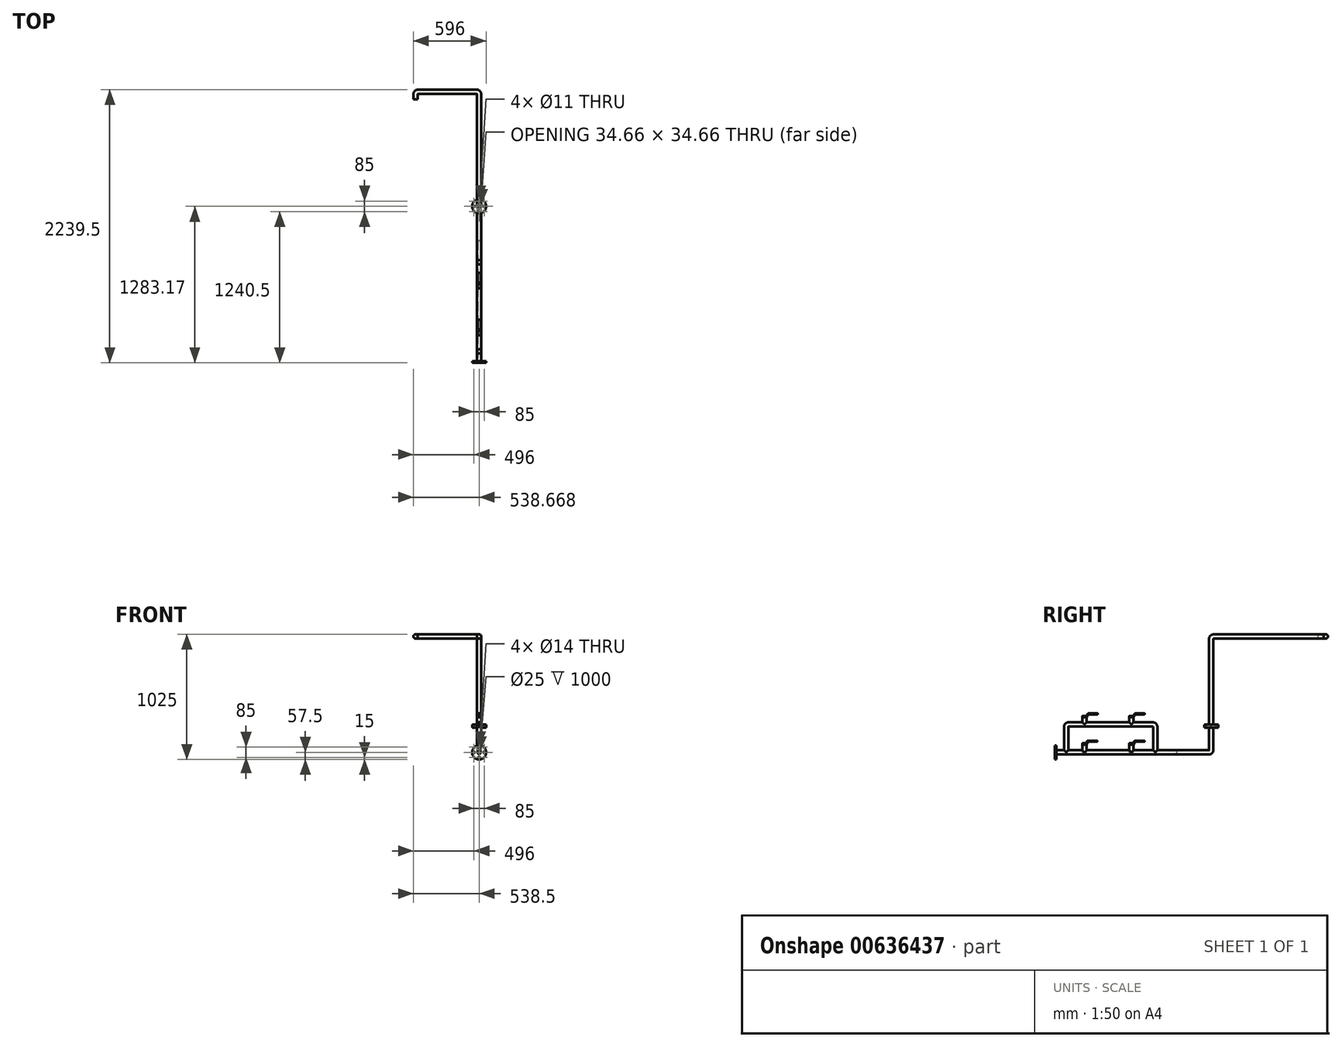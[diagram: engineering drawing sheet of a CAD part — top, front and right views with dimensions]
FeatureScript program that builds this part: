
annotation { "Feature Type Name" : "Feature", "Feature Type Description" : "" }
export const myFeature = defineFeature(function(context is Context, id is Id, definition is map)
    precondition{}
    {
        {
            var Q0;
            Q0=qCreatedBy(makeId("Front.planeOp"),FACE);
            var sketch = newSketch(context, id + "F0", { "sketchPlane" : qUnion([Q0])});
            skCircle(sketch, "E0", {"center": v(0, 0) * mm, "radius": 17.5 * mm});
            skSolve(sketch);
        }
        {
            var Q0;
            Q0=qCreatedBy(makeId("Top.planeOp"),FACE);
            var sketch = newSketch(context, id + "F1", { "sketchPlane" : qUnion([Q0])});
            skLineSegment(sketch, "E1", {"start": v(0, 0) * mm, "end": v(0, 43) * mm});
            skLineSegment(sketch, "E2", {"start": v(20, 63) * mm, "end": v(501, 63) * mm});
            skLineSegment(sketch, "E3", {"start": v(521, 43) * mm, "end": v(521, -876) * mm});
            skPoint(sketch, "E4.visualSharp", {"position": v(0, 63) * mm});
            skArc(sketch, "E4.filletArc", {"start": v(20, 63) * mm, "mid": v(5.86, 57.14) * mm, "end": v(0, 43) * mm});
            skPoint(sketch, "E5.visualSharp", {"position": v(521, 63) * mm});
            skArc(sketch, "E5.filletArc", {"start": v(521, 43) * mm, "mid": v(515.14, 57.14) * mm, "end": v(501, 63) * mm});
            skSolve(sketch);
        }
        {
            var Q0;
            Q0=qCreatedBy(makeId("Right.planeOp"),FACE);
            cPlane(context, id + "F2", {"entities" : qUnion([Q0]), "cplaneType" : CPlaneType.OFFSET, "offset" : 521 * mm, "width" : 150 * mm, "height" : 150 * mm});
        }
        {
            var Q0;
            Q0=qCreatedBy(id+"F2.planeOp",FACE);
            var sketch = newSketch(context, id + "F3", { "sketchPlane" : qUnion([Q0])});
            skLineSegment(sketch, "E6.0", {"start": v(43, 0) * mm, "end": v(-856, 0) * mm});
            skLineSegment(sketch, "E7", {"start": v(-876, -20) * mm, "end": v(-876, -930) * mm});
            skLineSegment(sketch, "E8", {"start": v(-896, -950) * mm, "end": v(-2159, -950) * mm});
            skLineSegment(sketch, "E9", {"start": v(-2065, -950) * mm, "end": v(-2065, -741) * mm});
            skLineSegment(sketch, "E10", {"start": v(-2045, -721) * mm, "end": v(-1355, -721) * mm});
            skLineSegment(sketch, "E11", {"start": v(-1335, -741) * mm, "end": v(-1335, -950) * mm});
            skPoint(sketch, "E12.visualSharp", {"position": v(-876, 0) * mm});
            skArc(sketch, "E12.filletArc", {"start": v(-856, 0) * mm, "mid": v(-870.14, -5.86) * mm, "end": v(-876, -20) * mm});
            skPoint(sketch, "E13.visualSharp", {"position": v(-876, -950) * mm});
            skArc(sketch, "E13.filletArc", {"start": v(-896, -950) * mm, "mid": v(-881.86, -944.14) * mm, "end": v(-876, -930) * mm});
            skPoint(sketch, "E14.visualSharp", {"position": v(-1335, -721) * mm});
            skArc(sketch, "E14.filletArc", {"start": v(-1335, -741) * mm, "mid": v(-1340.86, -726.86) * mm, "end": v(-1355, -721) * mm});
            skPoint(sketch, "E15.visualSharp", {"position": v(-2065, -721) * mm});
            skArc(sketch, "E15.filletArc", {"start": v(-2045, -721) * mm, "mid": v(-2059.14, -726.86) * mm, "end": v(-2065, -741) * mm});
            skSolve(sketch);
        }
        {
            var Q0;
            Q0=makeQuery(id+"F0.imprint","IMPRINT",FACE,{"disambiguationData":[TD([[makeQuery(id+"F0.imprint","IMPRINT",EDGE,{"derivedFrom":sQuery(id+"F0.wireOp",EDGE,"E0")}),1.0]])]});
            var Q1;
            Q1=sQuery(id+"F1.wireOp",EDGE,"E1");
            var Q2;
            Q2=sQuery(id+"F1.wireOp",EDGE,"E4.filletArc");
            var Q3;
            Q3=sQuery(id+"F1.wireOp",EDGE,"E2");
            var Q4;
            Q4=sQuery(id+"F1.wireOp",EDGE,"E5.filletArc");
            var Q5;
            Q5=sQuery(id+"F3.wireOp",EDGE,"E6.0");
            var Q6;
            Q6=sQuery(id+"F3.wireOp",EDGE,"E12.filletArc");
            var Q7;
            Q7=sQuery(id+"F3.wireOp",EDGE,"E7");
            var Q8;
            Q8=sQuery(id+"F3.wireOp",EDGE,"E13.filletArc");
            var Q9;
            Q9=sQuery(id+"F3.wireOp",EDGE,"E8");
            sweep(context, id + "F4", {"profiles" : qUnion([Q0]), "path" : qUnion([Q1, Q2, Q3, Q4, Q5, Q6, Q7, Q8, Q9])});
        }
        {
            var Q0;
            Q0=qCreatedBy(makeId("Top.planeOp"),FACE);
            cPlane(context, id + "F5", {"entities" : qUnion([Q0]), "cplaneType" : CPlaneType.OFFSET, "offset" : 886 * mm, "oppositeDirection" : true, "width" : 150 * mm, "height" : 150 * mm});
        }
        {
            var Q0;
            Q0=qCreatedBy(id+"F5.planeOp",FACE);
            var sketch = newSketch(context, id + "F6", { "sketchPlane" : qUnion([Q0])});
            skPoint(sketch, "E16.0", {"position": v(521, -2065) * mm});
            skPoint(sketch, "E17.0", {"position": v(521, -2059.14) * mm});
            skCircle(sketch, "E18", {"center": v(521, -2065) * mm, "radius": 17.5 * mm});
            skSolve(sketch);
        }
        {
            var Q0;
            Q0 = qSketchRegion(id + "F6", true);
            var Q1;
            Q1=sQuery(id+"F3.wireOp",EDGE,"E9");
            var Q2;
            Q2=sQuery(id+"F3.wireOp",EDGE,"E15.filletArc");
            var Q3;
            Q3=sQuery(id+"F3.wireOp",EDGE,"E10");
            var Q4;
            Q4=sQuery(id+"F3.wireOp",EDGE,"E14.filletArc");
            var Q5;
            Q5=sQuery(id+"F3.wireOp",EDGE,"E11");
            sweep(context, id + "F7", {"operationType" : NewBodyOperationType.ADD, "profiles" : qUnion([Q0]), "path" : qUnion([Q1, Q2, Q3, Q4, Q5])});
        }
        {
            var Q0;
            Q0=makeQuery(id+"F4.opSweep","CAP_FACE",FACE,{"disambiguationData":[OSD([sQuery(id+"F0.wireOp",EDGE,"E0"),sQuery(id+"F3.wireOp",VERTEX,"E8.end")])],"isStart":false});
            var sketch = newSketch(context, id + "F8", { "sketchPlane" : qUnion([Q0])});
            skCircle(sketch, "E19", {"center": v(521, -950) * mm, "radius": 57.5 * mm});
            skCircle(sketch, "E20", {"center": v(521, -907.5) * mm, "radius": 7 * mm});
            skCircle(sketch, "E21.1.0", {"center": v(478.5, -950) * mm, "radius": 7 * mm});
            skCircle(sketch, "E21.2.0", {"center": v(521, -992.5) * mm, "radius": 7 * mm});
            skCircle(sketch, "E21.3.0", {"center": v(563.5, -950) * mm, "radius": 7 * mm});
            skSolve(sketch);
        }
        {
            var Q0;
            Q0=makeQuery(id+"F8.imprint","IMPRINT",FACE,{"disambiguationData":[TD([[makeQuery(id+"F8.imprint","IMPRINT",EDGE,{"derivedFrom":sQuery(id+"F8.wireOp",EDGE,"E19")}),1.0]])]});
            extrude(context, id + "F9", {"entities" : qUnion([Q0]), "operationType" : NewBodyOperationType.ADD, "oppositeDirection" : true, "depth" : 15 * mm, "offsetDistance" : 25 * mm});
        }
        {
            var Q0;
            {var subQ0=sQuery(id+"F3.wireOp",VERTEX,"E8.end");var subQ1=sQuery(id+"F0.wireOp",EDGE,"E0");Q0=makeQuery(id+"F9.boolean.opBoolean","MERGE",FACE,{"derivedFrom":[makeQuery(id+"F4.opSweep","CAP_FACE",FACE,{"disambiguationData":[OSD([subQ1,subQ0])],"isStart":false}),makeQuery(id+"F9.opExtrude","CAP_FACE",FACE,{"disambiguationData":[OSD([subQ1,subQ0,sQuery(id+"F8.wireOp",EDGE,"E19"),sQuery(id+"F8.wireOp",EDGE,"E20"),sQuery(id+"F8.wireOp",EDGE,"E21.1.0"),sQuery(id+"F8.wireOp",EDGE,"E21.2.0"),sQuery(id+"F8.wireOp",EDGE,"E21.3.0")])],"isStart":true})]});}
            var sketch = newSketch(context, id + "F10", { "sketchPlane" : qUnion([Q0])});
            skCircle(sketch, "E22", {"center": v(521, -950) * mm, "radius": 12.5 * mm});
            skSolve(sketch);
        }
        {
            var Q0;
            Q0=makeQuery(id+"F10.imprint","IMPRINT",FACE,{"disambiguationData":[TD([[makeQuery(id+"F10.imprint","IMPRINT",EDGE,{"derivedFrom":sQuery(id+"F10.wireOp",EDGE,"E22")}),1.0]])]});
            extrude(context, id + "F11", {"entities" : qUnion([Q0]), "operationType" : NewBodyOperationType.REMOVE, "oppositeDirection" : true, "depth" : 1000 * mm, "offsetDistance" : 25 * mm});
        }
        {
            var Q0;
            Q0=qCreatedBy(id+"F5.planeOp",FACE);
            var sketch = newSketch(context, id + "F12", { "sketchPlane" : qUnion([Q0])});
            skCircle(sketch, "E23", {"center": v(521, -1915) * mm, "radius": 17.5 * mm});
            skCircle(sketch, "E24", {"center": v(521, -1530) * mm, "radius": 17.5 * mm});
            skSolve(sketch);
        }
        {
            var Q0;
            Q0 = qSketchRegion(id + "F12", true);
            extrude(context, id + "F13", {"entities" : qUnion([Q0]), "operationType" : NewBodyOperationType.ADD, "oppositeDirection" : true, "depth" : 64 * mm, "offsetDistance" : 25 * mm});
        }
        {
            var Q0;
            Q0=qCreatedBy(id+"F2.planeOp",FACE);
            var sketch = newSketch(context, id + "F14", { "sketchPlane" : qUnion([Q0])});
            skLineSegment(sketch, "E25.0.0", {"start": v(-2065, -950) * mm, "end": v(-1335, -950) * mm});
            skLineSegment(sketch, "E25.0.1", {"start": v(-1335, -950) * mm, "end": v(-1335, -741) * mm});
            skArc(sketch, "E25.0.2", {"start": v(-1335, -741) * mm, "mid": v(-1340.86, -726.86) * mm, "end": v(-1355, -721) * mm});
            skLineSegment(sketch, "E25.0.3", {"start": v(-1355, -721) * mm, "end": v(-2045, -721) * mm});
            skArc(sketch, "E25.0.4", {"start": v(-2045, -721) * mm, "mid": v(-2059.14, -726.86) * mm, "end": v(-2065, -741) * mm});
            skLineSegment(sketch, "E25.0.5", {"start": v(-2065, -741) * mm, "end": v(-2065, -950) * mm});
            skLineSegment(sketch, "E26.0", {"start": v(-1932.5, -886) * mm, "end": v(-1897.5, -886) * mm});
            skLineSegment(sketch, "E27", {"start": v(-1932.5, -886) * mm, "end": v(-1932.5, -876) * mm});
            skLineSegment(sketch, "E28", {"start": v(-1932.5, -876) * mm, "end": v(-1899.5, -876) * mm});
            skLineSegment(sketch, "E29", {"start": v(-1899.5, -876) * mm, "end": v(-1888.61, -853.8) * mm});
            skLineSegment(sketch, "E30", {"start": v(-1888.61, -853.8) * mm, "end": v(-1808.61, -853.8) * mm});
            skLineSegment(sketch, "E31", {"start": v(-1808.61, -853.8) * mm, "end": v(-1808.61, -861.8) * mm});
            skLineSegment(sketch, "E32", {"start": v(-1808.61, -861.8) * mm, "end": v(-1885.61, -861.8) * mm});
            skLineSegment(sketch, "E33", {"start": v(-1885.61, -861.8) * mm, "end": v(-1897.5, -886) * mm});
            skLineSegment(sketch, "E34.0", {"start": v(-1547.5, -886) * mm, "end": v(-1512.5, -886) * mm});
            skLineSegment(sketch, "E35", {"start": v(-1547.5, -886) * mm, "end": v(-1547.5, -876) * mm});
            skLineSegment(sketch, "E36", {"start": v(-1547.5, -876) * mm, "end": v(-1513.5, -876) * mm});
            skLineSegment(sketch, "E37", {"start": v(-1513.5, -876) * mm, "end": v(-1501.7, -855.1) * mm});
            skLineSegment(sketch, "E38", {"start": v(-1501.7, -855.1) * mm, "end": v(-1421.7, -855.1) * mm});
            skLineSegment(sketch, "E39", {"start": v(-1421.7, -855.1) * mm, "end": v(-1421.7, -863.1) * mm});
            skLineSegment(sketch, "E40", {"start": v(-1421.7, -863.1) * mm, "end": v(-1499.7, -863.1) * mm});
            skLineSegment(sketch, "E41", {"start": v(-1499.7, -863.1) * mm, "end": v(-1512.5, -886) * mm});
            skSolve(sketch);
        }
        {
            var Q0;
            Q0=makeQuery(id+"F14.imprint","IMPRINT",FACE,{"disambiguationData":[TD([[makeQuery(id+"F14.imprint","IMPRINT",EDGE,{"derivedFrom":sQuery(id+"F14.wireOp",EDGE,"E26.0")}),1.0]])]});
            extrude(context, id + "F15", {"entities" : qUnion([Q0]), "operationType" : NewBodyOperationType.ADD, "endBound" : BoundingType.SYMMETRIC, "depth" : 25 * mm, "offsetDistance" : 25 * mm});
        }
        {
            var Q0;
            Q0=makeQuery(id+"F15.opExtrude","CAP_EDGE",EDGE,{"disambiguationData":[OSD([sQuery(id+"F14.wireOp",EDGE,"E27")])],"isStart":false});
            var Q1;
            Q1=makeQuery(id+"F15.opExtrude","CAP_EDGE",EDGE,{"disambiguationData":[OSD([sQuery(id+"F14.wireOp",EDGE,"E27")])],"isStart":true});
            var Q2;
            Q2=makeQuery(id+"F15.opExtrude","CAP_EDGE",EDGE,{"disambiguationData":[OSD([sQuery(id+"F14.wireOp",EDGE,"E31")])],"isStart":false});
            var Q3;
            Q3=makeQuery(id+"F15.opExtrude","CAP_EDGE",EDGE,{"disambiguationData":[OSD([sQuery(id+"F14.wireOp",EDGE,"E31")])],"isStart":true});
            fillet(context, id + "F16", {"entities" : qUnion([Q0, Q1, Q2, Q3]), "radius" : 10 * mm, "tangentPropagation" : true, "allowEdgeOverflow" : false});
        }
        {
            var Q0;
            Q0=makeQuery(id+"F15.opExtrude","CAP_EDGE",EDGE,{"disambiguationData":[OSD([sQuery(id+"F14.wireOp",EDGE,"E30")])],"isStart":false});
            var Q1;
            Q1=makeQuery(id+"F15.opExtrude","CAP_EDGE",EDGE,{"disambiguationData":[OSD([sQuery(id+"F14.wireOp",EDGE,"E32")])],"isStart":false});
            fillet(context, id + "F17", {"entities" : qUnion([Q0, Q1]), "radius" : 3 * mm, "tangentPropagation" : true, "allowEdgeOverflow" : false});
        }
        {
            var Q0;
            Q0=makeQuery(id+"F14.imprint","IMPRINT",FACE,{"disambiguationData":[TD([[makeQuery(id+"F14.imprint","IMPRINT",EDGE,{"derivedFrom":sQuery(id+"F14.wireOp",EDGE,"E34.0")}),1.0]])]});
            extrude(context, id + "F18", {"entities" : qUnion([Q0]), "operationType" : NewBodyOperationType.ADD, "endBound" : BoundingType.SYMMETRIC, "depth" : 25 * mm, "offsetDistance" : 25 * mm});
        }
        {
            var Q0;
            Q0=makeQuery(id+"F18.opExtrude","CAP_EDGE",EDGE,{"disambiguationData":[OSD([sQuery(id+"F14.wireOp",EDGE,"E35")])],"isStart":false});
            var Q1;
            Q1=makeQuery(id+"F18.opExtrude","CAP_EDGE",EDGE,{"disambiguationData":[OSD([sQuery(id+"F14.wireOp",EDGE,"E35")])],"isStart":true});
            var Q2;
            Q2=makeQuery(id+"F18.opExtrude","CAP_EDGE",EDGE,{"disambiguationData":[OSD([sQuery(id+"F14.wireOp",EDGE,"E39")])],"isStart":false});
            var Q3;
            Q3=makeQuery(id+"F18.opExtrude","CAP_EDGE",EDGE,{"disambiguationData":[OSD([sQuery(id+"F14.wireOp",EDGE,"E39")])],"isStart":true});
            fillet(context, id + "F19", {"entities" : qUnion([Q0, Q1, Q2, Q3]), "radius" : 10 * mm, "tangentPropagation" : true, "allowEdgeOverflow" : false});
        }
        {
            var Q0;
            Q0=makeQuery(id+"F18.opExtrude","SWEPT_FACE",FACE,{"disambiguationData":[OSD([sQuery(id+"F14.wireOp",EDGE,"E38")])]});
            var Q1;
            Q1=makeQuery(id+"F18.opExtrude","CAP_EDGE",EDGE,{"disambiguationData":[OSD([sQuery(id+"F14.wireOp",EDGE,"E40")])],"isStart":false});
            fillet(context, id + "F20", {"entities" : qUnion([Q0, Q1]), "radius" : 4 * mm, "tangentPropagation" : true, "allowEdgeOverflow" : false});
        }
        {
            var Q0;
            Q0=qCreatedBy(id+"F5.planeOp",FACE);
            cPlane(context, id + "F21", {"entities" : qUnion([Q0]), "cplaneType" : CPlaneType.OFFSET, "offset" : 165 * mm, "width" : 150 * mm, "height" : 150 * mm});
        }
        {
            var Q0;
            Q0=qCreatedBy(id+"F21.planeOp",FACE);
            var sketch = newSketch(context, id + "F22", { "sketchPlane" : qUnion([Q0])});
            skArc(sketch, "E42.0", {"start": v(530.33, -1929.8) * mm, "mid": v(538.38, -1917.04) * mm, "end": v(533.5, -1902.75) * mm});
            skArc(sketch, "E43.0", {"start": v(508.5, -1902.75) * mm, "mid": v(503.62, -1917.04) * mm, "end": v(511.67, -1929.8) * mm});
            skArc(sketch, "E44.0", {"start": v(533.5, -1902.75) * mm, "mid": v(527.78, -1898.87) * mm, "end": v(521, -1897.5) * mm});
            skArc(sketch, "E45.0", {"start": v(521, -1897.5) * mm, "mid": v(514.22, -1898.87) * mm, "end": v(508.5, -1902.75) * mm});
            skArc(sketch, "E46.0", {"start": v(521, -1932.5) * mm, "mid": v(525.85, -1931.81) * mm, "end": v(530.33, -1929.8) * mm});
            skArc(sketch, "E47.0", {"start": v(511.67, -1929.8) * mm, "mid": v(516.15, -1931.81) * mm, "end": v(521, -1932.5) * mm});
            skArc(sketch, "E48.0", {"start": v(530.33, -1544.8) * mm, "mid": v(538.38, -1532.04) * mm, "end": v(533.5, -1517.75) * mm});
            skArc(sketch, "E49.0", {"start": v(521, -1547.5) * mm, "mid": v(525.85, -1546.81) * mm, "end": v(530.33, -1544.8) * mm});
            skArc(sketch, "E50.0", {"start": v(511.67, -1544.8) * mm, "mid": v(516.15, -1546.81) * mm, "end": v(521, -1547.5) * mm});
            skArc(sketch, "E51.0", {"start": v(533.5, -1517.75) * mm, "mid": v(527.78, -1513.87) * mm, "end": v(521, -1512.5) * mm});
            skArc(sketch, "E52.0", {"start": v(521, -1512.5) * mm, "mid": v(514.22, -1513.87) * mm, "end": v(508.5, -1517.75) * mm});
            skArc(sketch, "E53.0", {"start": v(508.5, -1517.75) * mm, "mid": v(503.62, -1532.04) * mm, "end": v(511.67, -1544.8) * mm});
            skSolve(sketch);
        }
        {
            var Q0;
            Q0 = qSketchRegion(id + "F22", true);
            extrude(context, id + "F23", {"entities" : qUnion([Q0]), "operationType" : NewBodyOperationType.ADD, "depth" : 60 * mm, "offsetDistance" : 25 * mm});
        }
        {
            var Q0;
            Q0=qCreatedBy(id+"F2.planeOp",FACE);
            var sketch = newSketch(context, id + "F24", { "sketchPlane" : qUnion([Q0])});
            skLineSegment(sketch, "E54.0", {"start": v(-1932.5, -661) * mm, "end": v(-1897.5, -661) * mm});
            skLineSegment(sketch, "E55.0", {"start": v(-1547.5, -661) * mm, "end": v(-1512.5, -661) * mm});
            skLineSegment(sketch, "E56", {"start": v(-1932.5, -661) * mm, "end": v(-1932.5, -651) * mm});
            skLineSegment(sketch, "E57", {"start": v(-1932.5, -651) * mm, "end": v(-1898.5, -651) * mm});
            skLineSegment(sketch, "E58", {"start": v(-1898.5, -651) * mm, "end": v(-1884.98, -629.97) * mm});
            skLineSegment(sketch, "E59", {"start": v(-1884.98, -629.97) * mm, "end": v(-1804.98, -629.97) * mm});
            skLineSegment(sketch, "E60", {"start": v(-1804.98, -629.97) * mm, "end": v(-1804.98, -637.97) * mm});
            skLineSegment(sketch, "E61", {"start": v(-1804.98, -637.97) * mm, "end": v(-1882.98, -637.97) * mm});
            skLineSegment(sketch, "E62", {"start": v(-1882.98, -637.97) * mm, "end": v(-1897.5, -661) * mm});
            skLineSegment(sketch, "E63", {"start": v(-1547.5, -661) * mm, "end": v(-1547.5, -651) * mm});
            skLineSegment(sketch, "E64", {"start": v(-1547.5, -651) * mm, "end": v(-1513.5, -651) * mm});
            skLineSegment(sketch, "E65", {"start": v(-1513.5, -651) * mm, "end": v(-1499.98, -629.97) * mm});
            skLineSegment(sketch, "E66", {"start": v(-1499.98, -629.97) * mm, "end": v(-1419.98, -629.97) * mm});
            skLineSegment(sketch, "E67", {"start": v(-1419.98, -629.97) * mm, "end": v(-1419.98, -637.97) * mm});
            skLineSegment(sketch, "E68", {"start": v(-1419.98, -637.97) * mm, "end": v(-1497.98, -637.97) * mm});
            skLineSegment(sketch, "E69", {"start": v(-1497.98, -637.97) * mm, "end": v(-1512.5, -661) * mm});
            skSolve(sketch);
        }
        {
            var Q0;
            Q0 = qSketchRegion(id + "F24", true);
            extrude(context, id + "F25", {"entities" : qUnion([Q0]), "operationType" : NewBodyOperationType.ADD, "endBound" : BoundingType.SYMMETRIC, "depth" : 25 * mm, "offsetDistance" : 25 * mm});
        }
        {
            var Q0;
            Q0=makeQuery(id+"F25.opExtrude","CAP_EDGE",EDGE,{"disambiguationData":[OSD([sQuery(id+"F24.wireOp",EDGE,"E56")])],"isStart":false});
            var Q1;
            Q1=makeQuery(id+"F25.opExtrude","CAP_EDGE",EDGE,{"disambiguationData":[OSD([sQuery(id+"F24.wireOp",EDGE,"E56")])],"isStart":true});
            var Q2;
            Q2=makeQuery(id+"F25.opExtrude","CAP_EDGE",EDGE,{"disambiguationData":[OSD([sQuery(id+"F24.wireOp",EDGE,"E60")])],"isStart":false});
            var Q3;
            Q3=makeQuery(id+"F25.opExtrude","CAP_EDGE",EDGE,{"disambiguationData":[OSD([sQuery(id+"F24.wireOp",EDGE,"E60")])],"isStart":true});
            var Q4;
            Q4=makeQuery(id+"F25.opExtrude","CAP_EDGE",EDGE,{"disambiguationData":[OSD([sQuery(id+"F24.wireOp",EDGE,"E67")])],"isStart":true});
            var Q5;
            Q5=makeQuery(id+"F25.opExtrude","CAP_EDGE",EDGE,{"disambiguationData":[OSD([sQuery(id+"F24.wireOp",EDGE,"E67")])],"isStart":false});
            var Q6;
            Q6=makeQuery(id+"F25.opExtrude","CAP_EDGE",EDGE,{"disambiguationData":[OSD([sQuery(id+"F24.wireOp",EDGE,"E63")])],"isStart":false});
            var Q7;
            Q7=makeQuery(id+"F25.opExtrude","CAP_EDGE",EDGE,{"disambiguationData":[OSD([sQuery(id+"F24.wireOp",EDGE,"E63")])],"isStart":true});
            fillet(context, id + "F26", {"entities" : qUnion([Q0, Q1, Q2, Q3, Q4, Q5, Q6, Q7]), "radius" : 10 * mm, "tangentPropagation" : true, "allowEdgeOverflow" : false});
        }
        {
            var Q0;
            Q0=makeQuery(id+"F25.opExtrude","CAP_EDGE",EDGE,{"disambiguationData":[OSD([sQuery(id+"F24.wireOp",EDGE,"E59")])],"isStart":false});
            var Q1;
            Q1=makeQuery(id+"F25.opExtrude","CAP_EDGE",EDGE,{"disambiguationData":[OSD([sQuery(id+"F24.wireOp",EDGE,"E61")])],"isStart":false});
            var Q2;
            Q2=makeQuery(id+"F25.opExtrude","CAP_EDGE",EDGE,{"disambiguationData":[OSD([sQuery(id+"F24.wireOp",EDGE,"E66")])],"isStart":false});
            var Q3;
            Q3=makeQuery(id+"F25.opExtrude","CAP_EDGE",EDGE,{"disambiguationData":[OSD([sQuery(id+"F24.wireOp",EDGE,"E68")])],"isStart":false});
            fillet(context, id + "F27", {"entities" : qUnion([Q0, Q1, Q2, Q3]), "radius" : 4 * mm, "tangentPropagation" : true, "allowEdgeOverflow" : false});
        }
        {
            var Q0;
            Q0=qCreatedBy(id+"F21.planeOp",FACE);
            var sketch = newSketch(context, id + "F28", { "sketchPlane" : qUnion([Q0])});
            skPoint(sketch, "E70.0", {"position": v(521, -876) * mm});
            skCircle(sketch, "E71", {"center": v(521, -876) * mm, "radius": 57.5 * mm});
            skCircle(sketch, "E72", {"center": v(521, -918.5) * mm, "radius": 5.5 * mm});
            skCircle(sketch, "E73.1.0", {"center": v(563.5, -876) * mm, "radius": 5.5 * mm});
            skCircle(sketch, "E73.2.0", {"center": v(521, -833.5) * mm, "radius": 5.5 * mm});
            skCircle(sketch, "E73.3.0", {"center": v(478.5, -876) * mm, "radius": 5.5 * mm});
            skSolve(sketch);
        }
        {
            var Q0;
            Q0=makeQuery(id+"F28.imprint","IMPRINT",FACE,{"disambiguationData":[TD([[makeQuery(id+"F28.imprint","IMPRINT",EDGE,{"derivedFrom":sQuery(id+"F28.wireOp",EDGE,"E71")}),1.0]])]});
            var Q1;
            Q1=sQuery(id+"F28.wireOp",EDGE,"E71");
            var Q2;
            Q2=sQuery(id+"F28.wireOp",EDGE,"E73.3.0");
            var Q3;
            Q3=sQuery(id+"F28.wireOp",EDGE,"E72");
            extrude(context, id + "F29", {"entities" : qUnion([Q0]), "operationType" : NewBodyOperationType.ADD, "surfaceEntities" : qUnion([Q1, Q2, Q3]), "oppositeDirection" : true, "depth" : 25 * mm, "offsetDistance" : 25 * mm});
        }
    });
